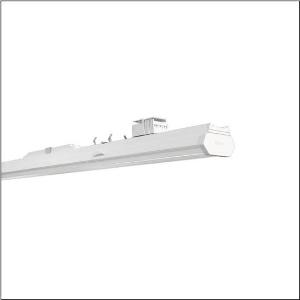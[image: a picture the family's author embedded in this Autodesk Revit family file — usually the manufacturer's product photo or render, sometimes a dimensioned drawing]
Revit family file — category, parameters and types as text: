
# Revit family: licross_r__11_protected_ho_51td11mn4gxs_4279
name_source: partatom
category: Lighting Fixtures
units: mm (PartAtom-declared; Revit-internal decimal feet)

## family parameters
Cut with Voids When Loaded = No
Host = Face
Light Source = No
Part Type = Normal
Room Calculation Point = No
Round Connector Dimension = Use Diameter
Shared = No

## types (1)
- --- (1 x LED, 16070 lm, 87.4 W, 4000K)
    Apparent Load = 87 VA
    CIE Flux Codes = 84 94 98 99 100
    Color Rendering = 80
    Color Temperature = 4000K
    Default Elevation = 1800 mm
    Description = Licross® 11 Protected HO, luminaire insert, of sheet steel, galvanised, coil coated, white, length: 1.500mm, width: 90mm, height: 101mm, LED rated luminous flux: 16.070lm, light colour: 840, control gear: ON/OFF Multilumen, with plug, 3-pole, with phase selection, mains connection: 220..240V, AC, 50/60Hz, rated input power: 87W, halogen-free wiring, primary light control with lens, of plastic, primary optical cover: cover, of PMMA, light emission: direct distribution, primary light characteristic: symmetric, protection rating (complete): IP54, insulation class (complete): insulation class I (protective earthing), certification: CE, ENEC, VDE, UKCA, protection symbol: D if used in an environment with non-conductive dust loads with corresponding accessories, impact resistance: IK06, permissible ambient temperature for indoor applications: -35..+35°C, corresponds to IFS (International Featured Standards) requirements for safety and quality in the food industry, reducing of maximum allowable ambient temperature of 5°C with ceiling mounting, LABS conformity tested according to VDMA 24364:2018-05, packaging unit: 1 piece
    Height = 92 mm
    Lamp = 1 x LED
    Lamp Light Flux = 16070 lm
    Lamp Power = 87.4 W
    Lamp count = 1
    Length = 1500 mm
    Luminous efficacy = 184 lm/W
    Manufacturer = Siteco
    ModVariant = No
    Model = 51TD11MN4GXS
    Mounting Place = Ceiling
    Mounting Type = Pendant
    Number of Poles = 1
    OnlyDefault = Yes
    Power Factor = 1
    Product Name = Licross® 11 Protected HO
    Product group = luminaire insert
    ProductGroupID = 901
    Protection Class = Protection class I
    Protection Degree = IP 54
    RLX_Detail_Level = 1
    RLX_Emergency_Light_Flux = 0 lm
    RLX_Emergency_Type = 0
    RLX_Emergency_Type_DB = No
    RlxData = <blob elided: 21997 chars, md5=47cad13d>
    Socket = socket
    Standby Power = 0 W
    System Light Flux = 16070 lm
    System Power = 87 W
    Type Comments = factory setting: luminous flux: 100 % | (A | C | E) | 203 mA
    Type Image = l_1256145.jpg
    URL = http://relux.com
    VarID = @adj_055219
    Voltage = 0 V
    Weight = 0.00 kg
    Width = 88 mm

## geometry (parser evidence)
native form markers: Blend x4, Sweep x13
no freeform markers — native parametric forms only
